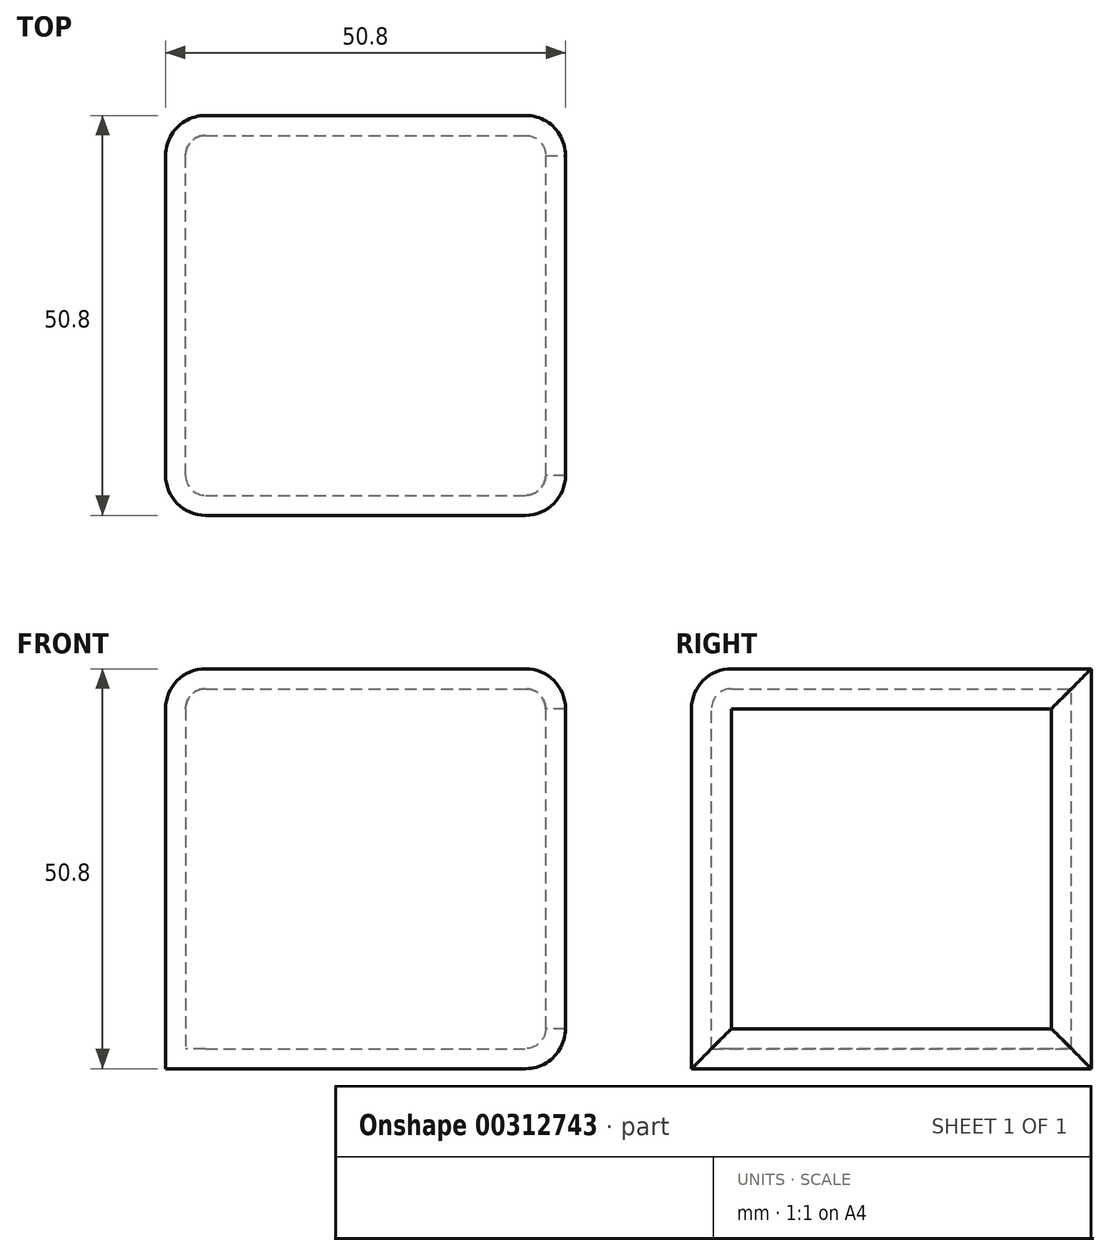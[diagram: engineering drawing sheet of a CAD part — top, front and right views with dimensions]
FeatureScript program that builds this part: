
annotation { "Feature Type Name" : "Feature", "Feature Type Description" : "" }
export const myFeature = defineFeature(function(context is Context, id is Id, definition is map)
    precondition{}
    {
        {
            var Q0;
            Q0=qCreatedBy(makeId("Top.planeOp"),FACE);
            var sketch = newSketch(context, id + "F0", { "sketchPlane" : qUnion([Q0])});
            skLineSegment(sketch, "E0", {"start": v(-54.42, -6.82) * mm, "end": v(-3.62, -6.82) * mm});
            skLineSegment(sketch, "E1", {"start": v(-3.62, -6.82) * mm, "end": v(-54.42, -6.82) * mm});
            skLineSegment(sketch, "E2", {"start": v(-54.42, -6.82) * mm, "end": v(-54.42, -57.62) * mm});
            skLineSegment(sketch, "E3", {"start": v(-54.42, -57.62) * mm, "end": v(-3.62, -57.62) * mm});
            skLineSegment(sketch, "E4", {"start": v(-3.62, -6.82) * mm, "end": v(-3.62, -57.62) * mm});
            skSolve(sketch);
        }
        {
            var Q0;
            Q0 = qSketchRegion(id + "F0", true);
            extrude(context, id + "F1", {"entities" : qUnion([Q0]), "depth" : 50.8 * mm, "offsetDistance" : 25.4 * mm});
        }
        {
            var Q0;
            Q0=makeQuery(id+"F1.opExtrude","SWEPT_FACE",FACE,{"disambiguationData":[OSD([sQuery(id+"F0.wireOp",EDGE,"E3")])]});
            var sketch = newSketch(context, id + "F2", { "sketchPlane" : qUnion([Q0])});
            skSolve(sketch);
        }
        {
            var Q0;
            Q0=makeQuery(id+"F1.opExtrude","CAP_EDGE",EDGE,{"disambiguationData":[OSD([sQuery(id+"F0.wireOp",EDGE,"E3")])],"isStart":false});
            var Q1;
            Q1=makeQuery(id+"F1.opExtrude","CAP_EDGE",EDGE,{"disambiguationData":[OSD([sQuery(id+"F0.wireOp",EDGE,"E2")])],"isStart":false});
            var Q2;
            Q2=makeQuery(id+"F1.opExtrude","CAP_EDGE",EDGE,{"disambiguationData":[OSD([sQuery(id+"F0.wireOp",EDGE,"E1")])],"isStart":false});
            var Q3;
            Q3=makeQuery(id+"F1.opExtrude","CAP_EDGE",EDGE,{"disambiguationData":[OSD([sQuery(id+"F0.wireOp",EDGE,"E4")])],"isStart":false});
            var Q4;
            Q4=makeQuery(id+"F1.opExtrude","SWEPT_EDGE",EDGE,{"disambiguationData":[OSD([sQuery(id+"F0.wireOp",EDGE,"E2"),sQuery(id+"F0.wireOp",EDGE,"E3")])]});
            var Q5;
            Q5=makeQuery(id+"F1.opExtrude","SWEPT_EDGE",EDGE,{"disambiguationData":[OSD([sQuery(id+"F0.wireOp",EDGE,"E1"),sQuery(id+"F0.wireOp",EDGE,"E2")])]});
            var Q6;
            Q6=makeQuery(id+"F1.opExtrude","SWEPT_EDGE",EDGE,{"disambiguationData":[OSD([sQuery(id+"F0.wireOp",EDGE,"E1"),sQuery(id+"F0.wireOp",EDGE,"E4")])]});
            var Q7;
            Q7=makeQuery(id+"F1.opExtrude","SWEPT_FACE",FACE,{"disambiguationData":[OSD([sQuery(id+"F0.wireOp",EDGE,"E4")])]});
            fillet(context, id + "F3", {"entities" : qUnion([Q0, Q1, Q2, Q3, Q4, Q5, Q6, Q7]), "radius" : 5.08 * mm, "tangentPropagation" : true, "allowEdgeOverflow" : false});
        }
        {
            var Q0;
            Q0=makeQuery(id+"F1.opExtrude","SWEPT_FACE",FACE,{"disambiguationData":[OSD([sQuery(id+"F0.wireOp",EDGE,"E4")])]});
            shell(context, id + "F4", {"entities" : qUnion([Q0]), "thickness" : 2.54 * mm});
        }
    });
